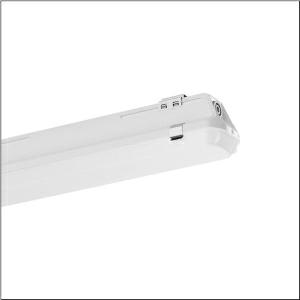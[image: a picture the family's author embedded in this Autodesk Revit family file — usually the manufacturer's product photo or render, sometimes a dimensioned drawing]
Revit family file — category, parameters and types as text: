
# Revit family: monsun_r__21_chemical_51fb30dp460b_d38f
name_source: partatom
category: Lighting Fixtures
units: mm (PartAtom-declared; Revit-internal decimal feet)

## family parameters
Cut with Voids When Loaded = No
Host = Face
Light Source = No
Part Type = Normal
Room Calculation Point = No
Round Connector Dimension = Use Diameter
Shared = No

## types (1)
- --- (1 x LED, 5740 lm, 39.4 W, 4000K)
    Apparent Load = 39 VA
    CIE Flux Codes = 48 77 93 95 100
    Color Rendering = 80
    Color Temperature = 4000K
    Default Elevation = 1800 mm
    Description = Monsun® 21 chemical, damp-proof luminaire, chain hanger, primary optical cover: enclosure, of PA, light emission: direct distribution, primary light characteristic: symmetric, installation type: suspended mounting, surface-mounted, horizontal mounting, vertical mounting, LED, rated luminous flux: 5.740lm, luminous efficacy: 146lm/W, light colour: 840, colour temperature: 4000K, control gear: ECG DALI, with terminal, 5-pole, max. 2.5mm², mains connection: 220..240V, AC, 50/60Hz, rated input power: 39W, housing, of glass-fibre reinforced polyester, uncoated, bright grey, incl. chain hanger, length: 1.590mm, width: 90mm, height: 88mm, clip for enclosure, of stainless steel (V2A), ceiling mounting element, of stainless steel (V2A), chain hanger, of stainless steel (V2A), protection rating (complete): IP66, insulation class (complete): insulation class I (protective earthing), certification: CE, ENEC, VDE, UKCA, protection symbol: D, impact resistance: IK08, permissible operating ambient temperature: -25..+35°C, standard: EN 50419, EN 60598-2-1, corresponds to IFS (International Featured Standards) requirements for safety and quality in the food industry, for indoor or canopied outdoor use, no direct snow, no direct sun, no direct rain, contact your sales advisor before using the luminaires in applications with unclear chemical exposure, large temperature fluctuations or condensation-forming humidity, LABS conformity tested according to VDMA 24364:2018-05, packaging unit: 1 piece
    Height = 89 mm
    Lamp = 1 x LED
    Lamp Light Flux = 5740 lm
    Lamp Power = 39.4 W
    Lamp count = 1
    Length = 1590 mm
    Luminous efficacy = 146 lm/W
    Manufacturer = Siteco
    ModVariant = No
    Model = 51FB30DP460B
    Mounting Place = Ceiling
    Mounting Type = Surface mounted
    Number of Poles = 1
    OnlyDefault = Yes
    Power Factor = 1
    Product Name = Monsun® 21 chemical
    Product group = damp-proof luminaire
    ProductGroupID = 300
    Protection Class = Protection class I
    Protection Degree = IP 66
    RLX_Detail_Level = 1
    RLX_Emergency_Light_Flux = 0 lm
    RLX_Emergency_Type = 0
    RLX_Emergency_Type_DB = No
    RlxData = <blob elided: 92573 chars, md5=223ee0ff>
    Socket = socket
    Standby Power = 0 W
    System Light Flux = 5740 lm
    System Power = 39 W
    Type Comments = factory setting: luminous flux: 100 % | dim-lin: 254 | 261 mA
    Type Image = l_1006717.jpg
    URL = http://relux.com
    VarID = @adj_134327
    Voltage = 0 V
    Weight = 0.00 kg
    Width = 90 mm

## geometry (parser evidence)
native form markers: Blend x4, Sweep x14
no freeform markers — native parametric forms only
